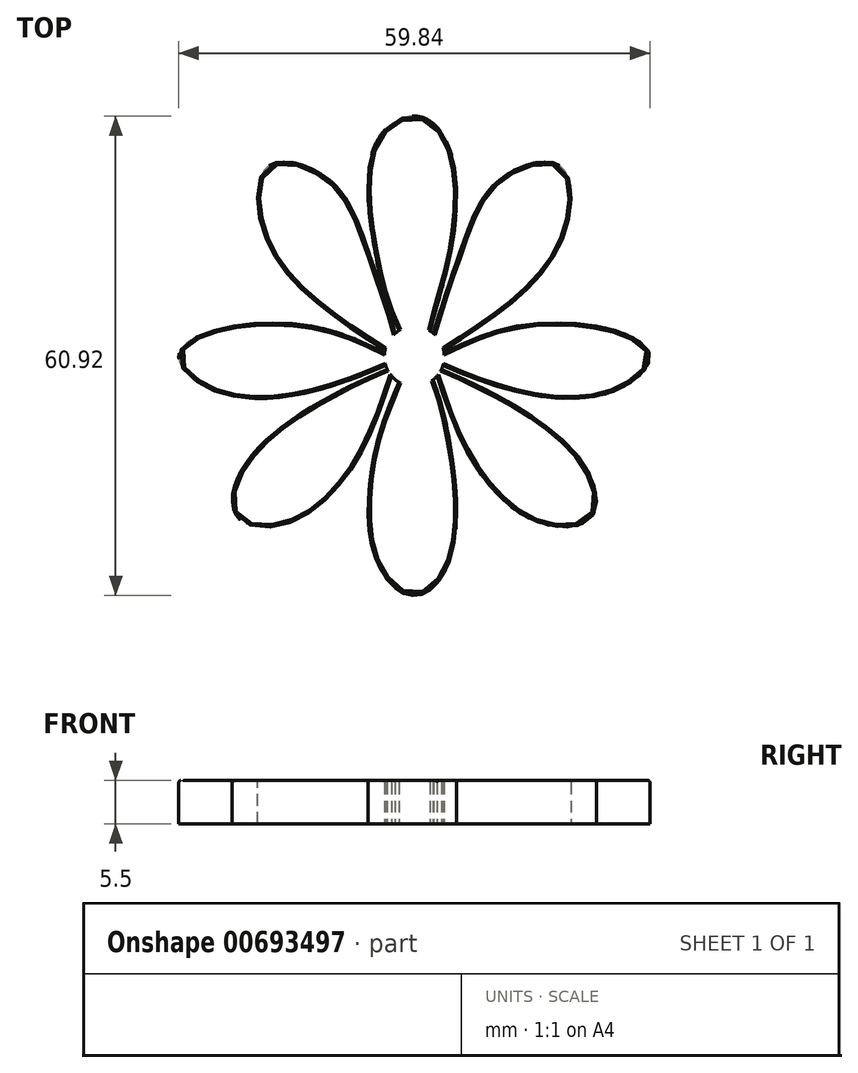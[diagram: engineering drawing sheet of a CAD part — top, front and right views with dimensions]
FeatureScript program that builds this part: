
annotation { "Feature Type Name" : "Feature", "Feature Type Description" : "" }
export const myFeature = defineFeature(function(context is Context, id is Id, definition is map)
    precondition{}
    {
        {
            var Q0;
            Q0=qCreatedBy(makeId("Top.planeOp"),FACE);
            var sketch = newSketch(context, id + "F0", { "sketchPlane" : qUnion([Q0])});
            skCircle(sketch, "E0", {"center": v(0, 0) * mm, "radius": 31.75 * mm});
            skArc(sketch, "E1", {"start": v(-2.86, -2.51) * mm, "mid": v(-2.44, -2.93) * mm, "end": v(-1.95, -3.27) * mm});
            skFitSpline(sketch, "E2", {"points": [v(-1.95, 3.27) * mm, v(-5.15, 14.12) * mm, v(-4.81, 27.23) * mm, v(0.31, 30.52) * mm, v(4.41, 26.56) * mm, v(4.84, 14.45) * mm, v(2.02, 3.23) * mm], "startDerivative": vector(-25.33, 52.01) * mm, "endDerivative": vector(-13.53, -55.17) * mm});
            skFitSpline(sketch, "E3", {"points": [v(2.45, 2.92) * mm, v(6.08, 14.02) * mm, v(10.81, 22.44) * mm, v(18.33, 24.3) * mm, v(19.72, 18) * mm, v(14.99, 9.23) * mm, v(3.73, 0.8) * mm], "startDerivative": vector(14, 52.75) * mm, "endDerivative": vector(-57.63, -37.4) * mm});
            skFitSpline(sketch, "E4", {"points": [v(-1.95, -3.27) * mm, v(-5.15, -12.66) * mm, v(-4.81, -25.9) * mm, v(0, -30.38) * mm, v(4.41, -26.1) * mm, v(4.84, -13.06) * mm, v(2.4, -2.96) * mm], "startDerivative": vector(-21.84, -51.57) * mm, "endDerivative": vector(-19.01, 50.57) * mm});
            skFitSpline(sketch, "E5", {"points": [v(3.78, 0.47) * mm, v(12.74, 3.78) * mm, v(25.23, 3.35) * mm, v(29.92, 0) * mm, v(25.34, -4.4) * mm, v(13.6, -4.6) * mm, v(3.63, -1.15) * mm], "startDerivative": vector(49.09, 23.85) * mm, "endDerivative": vector(-50.89, 20.87) * mm});
            skFitSpline(sketch, "E6", {"points": [v(2.86, -2.51) * mm, v(7.33, -13.2) * mm, v(15.55, -20.99) * mm, v(22.3, -20.61) * mm, v(22.5, -15.53) * mm, v(16.04, -8.38) * mm, v(3.44, -1.64) * mm], "startDerivative": vector(19.58, -57.19) * mm, "endDerivative": vector(-67.64, 28.82) * mm});
            skFitSpline(sketch, "E7.MirrorCS", {"points": [v(-3.78, 0.47) * mm, v(-12.74, 3.78) * mm, v(-25.23, 3.35) * mm, v(-29.92, 0) * mm, v(-25.34, -4.4) * mm, v(-13.6, -4.6) * mm, v(-3.63, -1.15) * mm], "startDerivative": vector(-49.09, 23.85) * mm, "endDerivative": vector(50.89, 20.87) * mm});
            skFitSpline(sketch, "E8.MirrorCS", {"points": [v(-2.86, -2.51) * mm, v(-7.33, -13.2) * mm, v(-15.55, -20.99) * mm, v(-22.3, -20.61) * mm, v(-22.5, -15.53) * mm, v(-16.04, -8.38) * mm, v(-3.44, -1.64) * mm], "startDerivative": vector(-19.58, -57.19) * mm, "endDerivative": vector(67.64, 28.82) * mm});
            skFitSpline(sketch, "E9.MirrorCS", {"points": [v(-2.45, 2.92) * mm, v(-6.08, 14.02) * mm, v(-10.81, 22.44) * mm, v(-18.33, 24.3) * mm, v(-19.72, 18) * mm, v(-14.99, 9.23) * mm, v(-3.73, 0.8) * mm], "startDerivative": vector(-14, 52.75) * mm, "endDerivative": vector(57.63, -37.4) * mm});
            skArc(sketch, "E10.trimOffspring", {"start": v(-3.63, -1.15) * mm, "mid": v(-3.54, -1.4) * mm, "end": v(-3.44, -1.64) * mm});
            skArc(sketch, "E11.trimOffspring", {"start": v(-3.73, 0.8) * mm, "mid": v(-3.76, 0.63) * mm, "end": v(-3.78, 0.47) * mm});
            skArc(sketch, "E12.trimOffspring", {"start": v(-1.95, 3.27) * mm, "mid": v(-2.2, 3.1) * mm, "end": v(-2.45, 2.92) * mm});
            skArc(sketch, "E13.trimOffspring", {"start": v(2.4, -2.96) * mm, "mid": v(2.64, -2.74) * mm, "end": v(2.86, -2.51) * mm});
            skArc(sketch, "E14.trimOffspring", {"start": v(3.78, 0.47) * mm, "mid": v(3.76, 0.63) * mm, "end": v(3.73, 0.8) * mm});
            skArc(sketch, "E15.trimOffspring", {"start": v(2.45, 2.92) * mm, "mid": v(2.24, 3.08) * mm, "end": v(2.02, 3.23) * mm});
            skArc(sketch, "E16.trimOffspring", {"start": v(3.44, -1.64) * mm, "mid": v(3.54, -1.4) * mm, "end": v(3.63, -1.15) * mm});
            skSolve(sketch);
        }
        {
            var Q0;
            {var subQ0=sQuery(id+"F0.wireOp",EDGE,"E6");Q0=makeQuery(id+"F0.imprint","IMPRINT",FACE,{"disambiguationData":[TD([[makeQuery(id+"F0.imprint","IMPRINT",EDGE,{"derivedFrom":subQ0}),1.0]])]});}
            var Q1;
            {var subQ0=sQuery(id+"F0.wireOp",EDGE,"E5");Q1=makeQuery(id+"F0.imprint","IMPRINT",FACE,{"disambiguationData":[TD([[makeQuery(id+"F0.imprint","IMPRINT",EDGE,{"derivedFrom":subQ0}),-1.0]])]});}
            var Q2;
            {var subQ0=sQuery(id+"F0.wireOp",EDGE,"E3");Q2=makeQuery(id+"F0.imprint","IMPRINT",FACE,{"disambiguationData":[TD([[makeQuery(id+"F0.imprint","IMPRINT",EDGE,{"derivedFrom":subQ0}),-1.0]])]});}
            var Q3;
            {var subQ0=sQuery(id+"F0.wireOp",EDGE,"E2");Q3=makeQuery(id+"F0.imprint","IMPRINT",FACE,{"disambiguationData":[TD([[makeQuery(id+"F0.imprint","IMPRINT",EDGE,{"derivedFrom":subQ0}),-1.0]])]});}
            var Q4;
            {var subQ0=sQuery(id+"F0.wireOp",EDGE,"E9.MirrorCS");Q4=makeQuery(id+"F0.imprint","IMPRINT",FACE,{"disambiguationData":[TD([[makeQuery(id+"F0.imprint","IMPRINT",EDGE,{"derivedFrom":subQ0}),1.0]])]});}
            var Q5;
            {var subQ0=sQuery(id+"F0.wireOp",EDGE,"E7.MirrorCS");Q5=makeQuery(id+"F0.imprint","IMPRINT",FACE,{"disambiguationData":[TD([[makeQuery(id+"F0.imprint","IMPRINT",EDGE,{"derivedFrom":subQ0}),1.0]])]});}
            var Q6;
            {var subQ0=sQuery(id+"F0.wireOp",EDGE,"E8.MirrorCS");Q6=makeQuery(id+"F0.imprint","IMPRINT",FACE,{"disambiguationData":[TD([[makeQuery(id+"F0.imprint","IMPRINT",EDGE,{"derivedFrom":subQ0}),-1.0]])]});}
            var Q7;
            {var subQ0=sQuery(id+"F0.wireOp",EDGE,"E4");Q7=makeQuery(id+"F0.imprint","IMPRINT",FACE,{"disambiguationData":[TD([[makeQuery(id+"F0.imprint","IMPRINT",EDGE,{"derivedFrom":subQ0}),1.0]])]});}
            var Q8;
            Q8=makeQuery(id+"F0.imprint","IMPRINT",FACE,{"disambiguationData":[TD([[makeQuery(id+"F0.imprint","IMPRINT",EDGE,{"derivedFrom":sQuery(id+"F0.wireOp",EDGE,"H32TxnIw-rBJC-nmNL-P1iF-2LgNU6qLi1U1")}),-1.0]])]});
            extrude(context, id + "F1", {"entities" : qUnion([Q0, Q1, Q2, Q3, Q4, Q5, Q6, Q7, Q8]), "depth" : 5.5 * mm, "offsetDistance" : 25.4 * mm});
        }
        {
            var Q0;
            Q0=makeQuery(id+"F1.opExtrude","CAP_EDGE",EDGE,{"disambiguationData":[OSD([sQuery(id+"F0.wireOp",EDGE,"E5")])],"isStart":false});
            var Q1;
            Q1=makeQuery(id+"F1.opExtrude","CAP_EDGE",EDGE,{"disambiguationData":[OSD([sQuery(id+"F0.wireOp",EDGE,"E6")])],"isStart":false});
            var Q2;
            Q2=makeQuery(id+"F1.opExtrude","CAP_EDGE",EDGE,{"disambiguationData":[OSD([sQuery(id+"F0.wireOp",EDGE,"E4")])],"isStart":false});
            var Q3;
            Q3=makeQuery(id+"F1.opExtrude","CAP_EDGE",EDGE,{"disambiguationData":[OSD([sQuery(id+"F0.wireOp",EDGE,"E8.MirrorCS")])],"isStart":false});
            var Q4;
            Q4=makeQuery(id+"F1.opExtrude","CAP_EDGE",EDGE,{"disambiguationData":[OSD([sQuery(id+"F0.wireOp",EDGE,"E7.MirrorCS")])],"isStart":false});
            var Q5;
            Q5=makeQuery(id+"F1.opExtrude","CAP_EDGE",EDGE,{"disambiguationData":[OSD([sQuery(id+"F0.wireOp",EDGE,"E9.MirrorCS")])],"isStart":false});
            var Q6;
            Q6=makeQuery(id+"F1.opExtrude","CAP_EDGE",EDGE,{"disambiguationData":[OSD([sQuery(id+"F0.wireOp",EDGE,"E2")])],"isStart":false});
            var Q7;
            Q7=makeQuery(id+"F1.opExtrude","CAP_EDGE",EDGE,{"disambiguationData":[OSD([sQuery(id+"F0.wireOp",EDGE,"E3")])],"isStart":false});
            fillet(context, id + "F2", {"entities" : qUnion([Q0, Q1, Q2, Q3, Q4, Q5, Q6, Q7]), "radius" : 0.25 * mm, "tangentPropagation" : true, "allowEdgeOverflow" : false});
        }
    });
